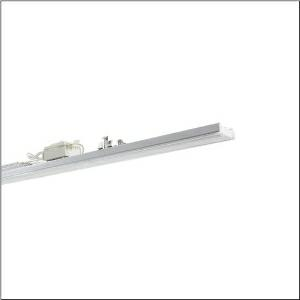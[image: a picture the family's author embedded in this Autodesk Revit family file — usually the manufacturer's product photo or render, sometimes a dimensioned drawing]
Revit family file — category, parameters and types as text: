
# Revit family: licross_21_recessed_mo_52tl12dn195g
name_source: partatom
category: Lighting Fixtures
units: mm (PartAtom-declared; Revit-internal decimal feet)

## family parameters
Cut with Voids When Loaded = No
Host = Face
Light Source = No
Part Type = Normal
Room Calculation Point = No
Round Connector Dimension = Use Diameter
Shared = No

## types (1)
- --- (1 x LED, 9950 lm, 58 W, 3500K)
    Apparent Load = 58 VA
    CIE Flux Codes = 72 92 99 100 100
    Color Rendering = 80
    Color Temperature = 3500K
    Default Elevation = 1800 mm
    Description = Licross 21 Recessed MO, luminaire insert, of sheet steel, galvanised, coil coated, white, length: 1.500mm, width: 66mm, height: 67mm, LED rated luminous flux: 9.950lm, light colour: 835, SDCM (Standard Deviation of Colour Matching)MacAdam ≤ 3 SDCM (initial), control gear: DALI 2, with plug, 5-pole, with phase selection, mains connection: 220..240V, AC, 50/60Hz, rated input power: 58W, internal wiring halogen-free, primary optical cover: cover, of PMMA, light emission: direct distribution, primary light characteristic: symmetric, protection rating (complete): IP40, insulation class (complete): insulation class I (protective earthing), certification: CE, ENEC, VDE, UKCA, protection symbol: D if used in an environment without relevant dust loads with corresponding accessories, impact resistance: IK06, permissible ambient temperature for indoor applications: -25..+35°C, corresponds to IFS (International Featured Standards) requirements for safety and quality in the food industry, reducing of maximum allowable ambient temperature of 5°C with ceiling mounting, LABS conformity tested according to VDMA 24364:2018-05, The light source and the operating device comply with the requirements of the Ecodesign Regulation (EU) 2019/2020 and are replaceable in accordance with this regulation, packaging unit: 1 piece
    Height = 58 mm
    Lamp = 1 x LED
    Lamp Light Flux = 9950 lm
    Lamp Power = 58 W
    Lamp count = 1
    Length = 1500 mm
    Luminous efficacy = 172 lm/W
    Manufacturer = Siteco
    ModVariant = No
    Model = 52TL12DN195G
    Mounting Place = Ceiling
    Mounting Type = Pendant
    Number of Poles = 1
    OnlyDefault = Yes
    Power Factor = 1
    Product Name = Licross 21 Recessed MO
    Product group = luminaire insert | ceiling pendant
    ProductGroupID = 901
    Protection Class = Protection class I
    Protection Degree = IP 40
    RLX_Detail_Level = 1
    RLX_Emergency_Light_Flux = 0 lm
    RLX_Emergency_Type = 0
    RLX_Emergency_Type_DB = No
    RlxData = <blob elided: 24889 chars, md5=919c72b3>
    Socket = socket
    Standby Power = 0 W
    System Light Flux = 9950 lm
    System Power = 58 W
    Type Comments = factory setting: luminous flux: 100 % | dim-lin: 254 | 390 mA
    Type Image = l_1296930.jpg
    URL = http://relux.com
    VarID = @adj_093503
    Voltage = 0 V
    Weight = 0.00 kg
    Width = 66 mm

## geometry (parser evidence)
native form markers: Blend x4, Sweep x12
no freeform markers — native parametric forms only
